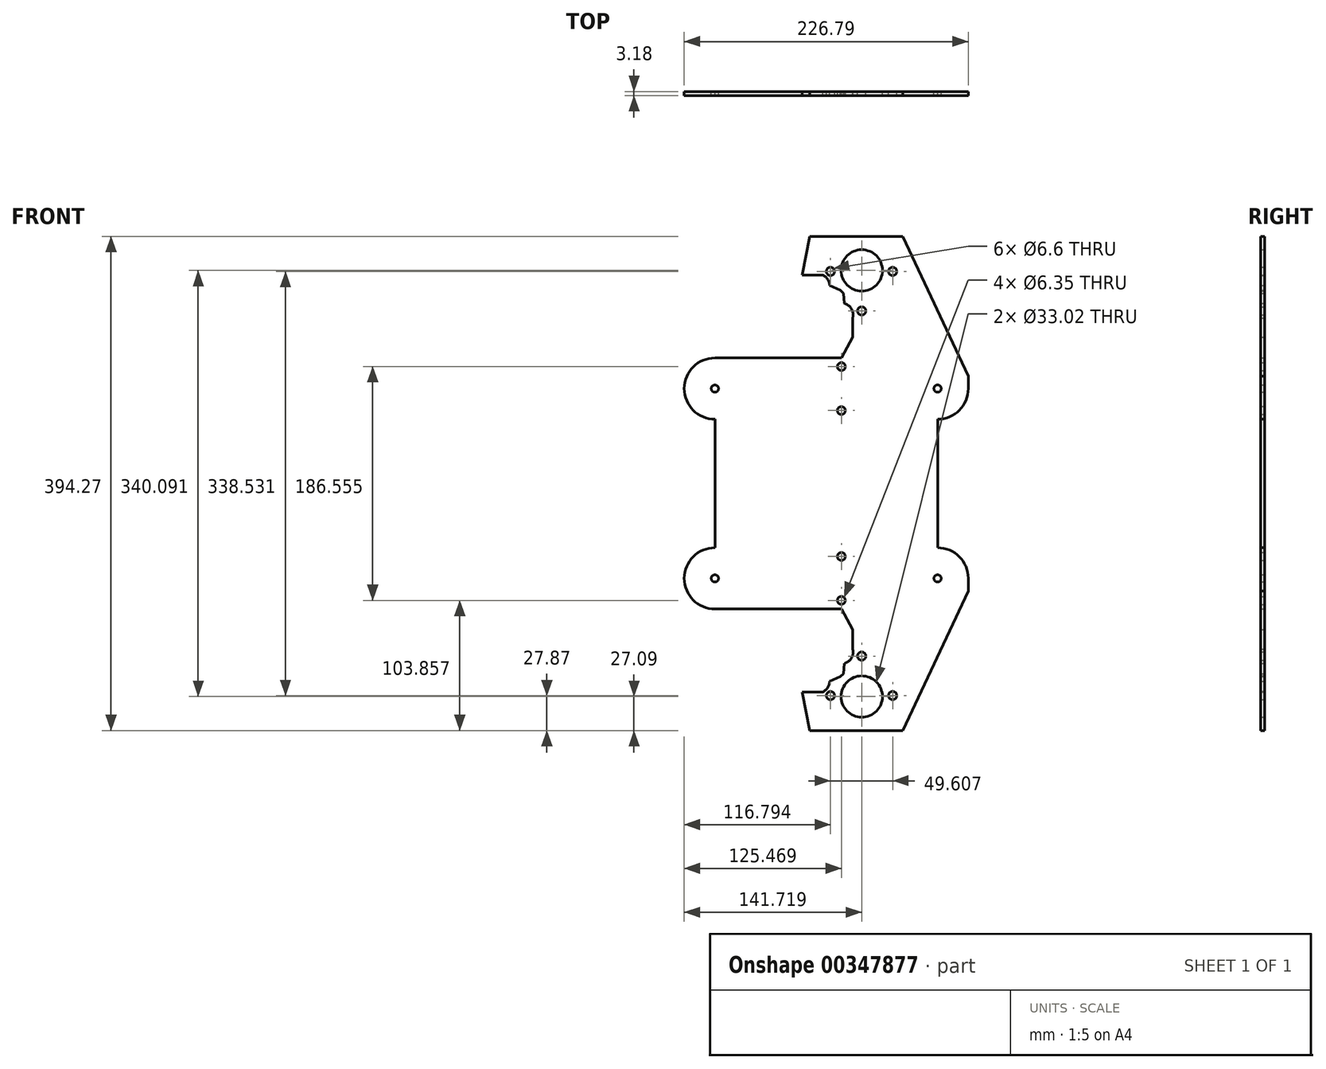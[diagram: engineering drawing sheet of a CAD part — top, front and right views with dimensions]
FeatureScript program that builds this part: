
annotation { "Feature Type Name" : "Feature", "Feature Type Description" : "" }
export const myFeature = defineFeature(function(context is Context, id is Id, definition is map)
    precondition{}
    {
        {
            var Q0;
            Q0=qCreatedBy(makeId("Front.planeOp"),FACE);
            var sketch = newSketch(context, id + "F0", { "sketchPlane" : qUnion([Q0])});
            skCircle(sketch, "E0", {"center": v(-4.64, -22.46) * mm, "radius": 3.17 * mm});
            skLineSegment(sketch, "E1", {"start": v(-4.64, -19.28) * mm, "end": v(-4.64, -15.53) * mm, "construction": true});
            skCircle(sketch, "E2", {"center": v(-4.64, -57.5) * mm, "radius": 3.18 * mm});
            skPoint(sketch, "E3", {"position": v(72.17, -39.98) * mm});
            skArc(sketch, "E4", {"start": v(72.17, -64.5) * mm, "mid": v(89.5, -57.32) * mm, "end": v(96.68, -39.98) * mm});
            skLineSegment(sketch, "E5", {"start": v(72.17, -76.84) * mm, "end": v(72.17, -64.5) * mm});
            skLineSegment(sketch, "E6", {"start": v(-19.49, 50.67) * mm, "end": v(-36, 50.68) * mm});
            skArc(sketch, "E7", {"start": v(-13.97, 42.17) * mm, "mid": v(-15.58, 47.16) * mm, "end": v(-19.49, 50.67) * mm});
            skLineSegment(sketch, "E8", {"start": v(-2.36, 27.9) * mm, "end": v(-2.9, 36.1) * mm});
            skLineSegment(sketch, "E9", {"start": v(-2.9, 36.1) * mm, "end": v(-5.4, 38.35) * mm});
            skLineSegment(sketch, "E10", {"start": v(-5.4, 38.35) * mm, "end": v(-13.97, 42.17) * mm});
            skCircle(sketch, "E11", {"center": v(-13.32, 53.53) * mm, "radius": 3.3 * mm});
            skCircle(sketch, "E12", {"center": v(11.54, 22) * mm, "radius": 3.3 * mm});
            skCircle(sketch, "E13", {"center": v(36.3, 53.5) * mm, "radius": 3.3 * mm});
            skCircle(sketch, "E14", {"center": v(11.6, 54.31) * mm, "radius": 16.51 * mm});
            skLineSegment(sketch, "E15", {"start": v(4.29, 1.01) * mm, "end": v(-4.64, -15.53) * mm});
            skLineSegment(sketch, "E16", {"start": v(-29.95, 81.4) * mm, "end": v(-36, 50.68) * mm});
            skLineSegment(sketch, "E17", {"start": v(96.68, -39.98) * mm, "end": v(96.68, -30.06) * mm});
            skPoint(sketch, "E18", {"position": v(-4.64, 18.83) * mm});
            skArc(sketch, "E19", {"start": v(-2.36, 27.9) * mm, "mid": v(3.44, 23.54) * mm, "end": v(4.37, 16.35) * mm});
            skLineSegment(sketch, "E20", {"start": v(4.29, 16.25) * mm, "end": v(4.37, 16.35) * mm});
            skLineSegment(sketch, "E21", {"start": v(-29.95, 81.4) * mm, "end": v(44.47, 81.4) * mm});
            skLineSegment(sketch, "E22", {"start": v(33.12, 53.5) * mm, "end": v(39.47, 53.5) * mm});
            skLineSegment(sketch, "E23", {"start": v(36.3, 56.67) * mm, "end": v(36.3, 50.32) * mm});
            skLineSegment(sketch, "E24", {"start": v(-16.5, 53.53) * mm, "end": v(-10.14, 53.53) * mm});
            skLineSegment(sketch, "E25", {"start": v(-13.32, 56.7) * mm, "end": v(-13.32, 50.36) * mm});
            skLineSegment(sketch, "E26", {"start": v(8.37, 22) * mm, "end": v(14.72, 22) * mm});
            skLineSegment(sketch, "E27", {"start": v(11.54, 25.18) * mm, "end": v(11.54, 18.83) * mm});
            skLineSegment(sketch, "E28", {"start": v(72.17, -64.5) * mm, "end": v(72.17, -15.53) * mm, "construction": true});
            skLineSegment(sketch, "E29", {"start": v(72.17, -15.53) * mm, "end": v(-4.64, -15.53) * mm, "construction": true});
            skCircle(sketch, "E30", {"center": v(-105.63, -40.01) * mm, "radius": 2.9 * mm});
            skLineSegment(sketch, "E31", {"start": v(4.29, 1.01) * mm, "end": v(4.37, 16.35) * mm});
            skLineSegment(sketch, "E32", {"start": v(-105.63, -64.5) * mm, "end": v(-105.63, -15.53) * mm, "construction": true});
            skLineSegment(sketch, "E33", {"start": v(-105.63, -15.53) * mm, "end": v(-4.64, -15.53) * mm});
            skArc(sketch, "E34", {"start": v(-105.63, -64.5) * mm, "mid": v(-130.11, -40.01) * mm, "end": v(-105.63, -15.53) * mm});
            skLineSegment(sketch, "E35", {"start": v(-105.63, -64.5) * mm, "end": v(-4.64, -64.5) * mm});
            skLineSegment(sketch, "E36", {"start": v(-4.64, -64.5) * mm, "end": v(72.17, -64.5) * mm});
            skCircle(sketch, "E37", {"center": v(72.17, -39.98) * mm, "radius": 2.9 * mm});
            skLineSegment(sketch, "E38", {"start": v(72.17, -76.84) * mm, "end": v(72.17, -154.63) * mm});
            skLineSegment(sketch, "E39", {"start": v(-105.63, -64.5) * mm, "end": v(-105.63, -76.84) * mm});
            skLineSegment(sketch, "E40", {"start": v(-105.63, -76.84) * mm, "end": v(-105.63, -154.63) * mm});
            skLineSegment(sketch, "E41", {"start": v(-105.63, -76.84) * mm, "end": v(72.17, -76.84) * mm});
            skLineSegment(sketch, "E42", {"start": v(-105.63, -154.63) * mm, "end": v(72.17, -154.63) * mm});
            skLineSegment(sketch, "E43", {"start": v(-105.63, -115.73) * mm, "end": v(72.17, -115.73) * mm, "construction": true});
            skLineSegment(sketch, "E44", {"start": v(-108.8, -40.01) * mm, "end": v(-102.45, -40.01) * mm});
            skLineSegment(sketch, "E45", {"start": v(-105.63, -36.84) * mm, "end": v(-105.63, -43.19) * mm});
            skLineSegment(sketch, "E46", {"start": v(69, -39.98) * mm, "end": v(75.35, -39.98) * mm});
            skLineSegment(sketch, "E47", {"start": v(72.17, -36.8) * mm, "end": v(72.17, -43.16) * mm});
            skLineSegment(sketch, "E48", {"start": v(-7.82, -57.5) * mm, "end": v(-1.47, -57.5) * mm});
            skLineSegment(sketch, "E49", {"start": v(-4.64, -54.33) * mm, "end": v(-4.64, -60.68) * mm});
            skLineSegment(sketch, "E50", {"start": v(-7.82, -22.46) * mm, "end": v(-1.47, -22.46) * mm});
            skLineSegment(sketch, "E51", {"start": v(-4.64, -19.28) * mm, "end": v(-4.64, -25.63) * mm});
            skLineSegment(sketch, "E52.MirrorCS", {"start": v(-4.64, -212.19) * mm, "end": v(-4.64, -205.84) * mm});
            skLineSegment(sketch, "E53.MirrorCS", {"start": v(-7.82, -209.01) * mm, "end": v(-1.47, -209.01) * mm});
            skLineSegment(sketch, "E54.MirrorCS", {"start": v(-4.64, -177.14) * mm, "end": v(-4.64, -170.79) * mm});
            skLineSegment(sketch, "E55.MirrorCS", {"start": v(69, -191.49) * mm, "end": v(75.35, -191.49) * mm});
            skLineSegment(sketch, "E56.MirrorCS", {"start": v(-7.82, -173.96) * mm, "end": v(-1.47, -173.96) * mm});
            skCircle(sketch, "E57.MirrorC", {"center": v(-4.64, -173.96) * mm, "radius": 3.18 * mm});
            skLineSegment(sketch, "E58.MirrorCS", {"start": v(-4.64, -212.19) * mm, "end": v(-4.64, -215.94) * mm, "construction": true});
            skCircle(sketch, "E59.MirrorC", {"center": v(-4.64, -209.01) * mm, "radius": 3.17 * mm});
            skLineSegment(sketch, "E60.MirrorCS", {"start": v(72.17, -194.66) * mm, "end": v(72.17, -188.31) * mm});
            skCircle(sketch, "E61.MirrorC", {"center": v(72.17, -191.49) * mm, "radius": 2.9 * mm});
            skLineSegment(sketch, "E62.MirrorCS", {"start": v(-108.8, -191.46) * mm, "end": v(-102.45, -191.46) * mm});
            skLineSegment(sketch, "E63.MirrorCS", {"start": v(-105.63, -194.63) * mm, "end": v(-105.63, -188.28) * mm});
            skLineSegment(sketch, "E64.MirrorCS", {"start": v(8.37, -253.47) * mm, "end": v(14.72, -253.47) * mm});
            skLineSegment(sketch, "E65.MirrorCS", {"start": v(-13.32, -288.18) * mm, "end": v(-13.32, -281.83) * mm});
            skCircle(sketch, "E66.MirrorC", {"center": v(-105.63, -191.46) * mm, "radius": 2.9 * mm});
            skLineSegment(sketch, "E67.MirrorCS", {"start": v(-16.5, -285) * mm, "end": v(-10.14, -285) * mm});
            skLineSegment(sketch, "E68.MirrorCS", {"start": v(11.54, -256.65) * mm, "end": v(11.54, -250.3) * mm});
            skCircle(sketch, "E69.MirrorC", {"center": v(11.54, -253.47) * mm, "radius": 3.3 * mm});
            skCircle(sketch, "E70.MirrorC", {"center": v(-13.32, -285) * mm, "radius": 3.3 * mm});
            skLineSegment(sketch, "E71.MirrorCS", {"start": v(4.29, -247.72) * mm, "end": v(4.37, -247.82) * mm});
            skArc(sketch, "E72.MirrorCS", {"start": v(-2.36, -259.37) * mm, "mid": v(3.44, -255.01) * mm, "end": v(4.37, -247.82) * mm});
            skLineSegment(sketch, "E73.MirrorCS", {"start": v(33.12, -284.97) * mm, "end": v(39.47, -284.97) * mm});
            skLineSegment(sketch, "E74.MirrorCS", {"start": v(36.3, -288.14) * mm, "end": v(36.3, -281.8) * mm});
            skCircle(sketch, "E75.MirrorC", {"center": v(36.3, -284.97) * mm, "radius": 3.3 * mm});
            skArc(sketch, "E76.MirrorCS", {"start": v(-13.97, -273.64) * mm, "mid": v(-15.58, -278.63) * mm, "end": v(-19.49, -282.14) * mm});
            skLineSegment(sketch, "E77.MirrorCS", {"start": v(4.29, -232.48) * mm, "end": v(4.37, -247.82) * mm});
            skLineSegment(sketch, "E78.MirrorCS", {"start": v(96.68, -191.49) * mm, "end": v(96.68, -201.41) * mm});
            skLineSegment(sketch, "E79.MirrorCS", {"start": v(-5.4, -269.82) * mm, "end": v(-13.97, -273.64) * mm});
            skLineSegment(sketch, "E80.MirrorCS", {"start": v(-2.9, -267.57) * mm, "end": v(-5.4, -269.82) * mm});
            skLineSegment(sketch, "E81.MirrorCS", {"start": v(-2.36, -259.37) * mm, "end": v(-2.9, -267.57) * mm});
            skLineSegment(sketch, "E82.MirrorCS", {"start": v(-19.49, -282.14) * mm, "end": v(-36, -282.15) * mm});
            skLineSegment(sketch, "E83.MirrorCS", {"start": v(4.29, -232.48) * mm, "end": v(-4.64, -215.94) * mm});
            skArc(sketch, "E84.MirrorCS", {"start": v(-105.63, -166.98) * mm, "mid": v(-130.11, -191.46) * mm, "end": v(-105.63, -215.94) * mm});
            skLineSegment(sketch, "E85.MirrorCS", {"start": v(-105.63, -215.94) * mm, "end": v(-4.64, -215.94) * mm});
            skLineSegment(sketch, "E86.MirrorCS", {"start": v(72.17, -166.98) * mm, "end": v(72.17, -215.94) * mm, "construction": true});
            skLineSegment(sketch, "E87.MirrorCS", {"start": v(-105.63, -166.98) * mm, "end": v(-105.63, -215.94) * mm, "construction": true});
            skLineSegment(sketch, "E88.MirrorCS", {"start": v(-4.64, -166.98) * mm, "end": v(72.17, -166.98) * mm});
            skLineSegment(sketch, "E89.MirrorCS", {"start": v(72.17, -215.94) * mm, "end": v(-4.64, -215.94) * mm, "construction": true});
            skLineSegment(sketch, "E90.MirrorCS", {"start": v(-29.95, -312.87) * mm, "end": v(44.47, -312.87) * mm});
            skArc(sketch, "E91.MirrorCS", {"start": v(72.17, -166.98) * mm, "mid": v(89.5, -174.15) * mm, "end": v(96.68, -191.49) * mm});
            skLineSegment(sketch, "E92.MirrorCS", {"start": v(-29.95, -312.87) * mm, "end": v(-36, -282.15) * mm});
            skCircle(sketch, "E93.MirrorC", {"center": v(11.6, -285.78) * mm, "radius": 16.51 * mm});
            skLineSegment(sketch, "E94.MirrorCS", {"start": v(-105.63, -166.98) * mm, "end": v(-4.64, -166.98) * mm});
            skLineSegment(sketch, "E95", {"start": v(-105.63, -166.98) * mm, "end": v(-105.63, -154.63) * mm});
            skLineSegment(sketch, "E96", {"start": v(72.17, -166.98) * mm, "end": v(72.17, -154.63) * mm});
            skLineSegment(sketch, "E97", {"start": v(44.47, -312.87) * mm, "end": v(96.68, -201.41) * mm});
            skLineSegment(sketch, "E98", {"start": v(44.47, 81.4) * mm, "end": v(96.68, -30.06) * mm});
            skSolve(sketch);
        }
        {
            var Q0;
            Q0=makeQuery(id+"F0.imprint","IMPRINT",FACE,{"disambiguationData":[TD([[makeQuery(id+"F0.imprint","IMPRINT",EDGE,{"derivedFrom":sQuery(id+"F0.wireOp",EDGE,"E0")}),-1.0]])]});
            var Q1;
            Q1=qSketchRegion(id+"F0",true);
            extrude(context, id + "F1", {"entities" : qUnion([Q0, Q1]), "depth" : 3.17 * mm});
        }
    });
